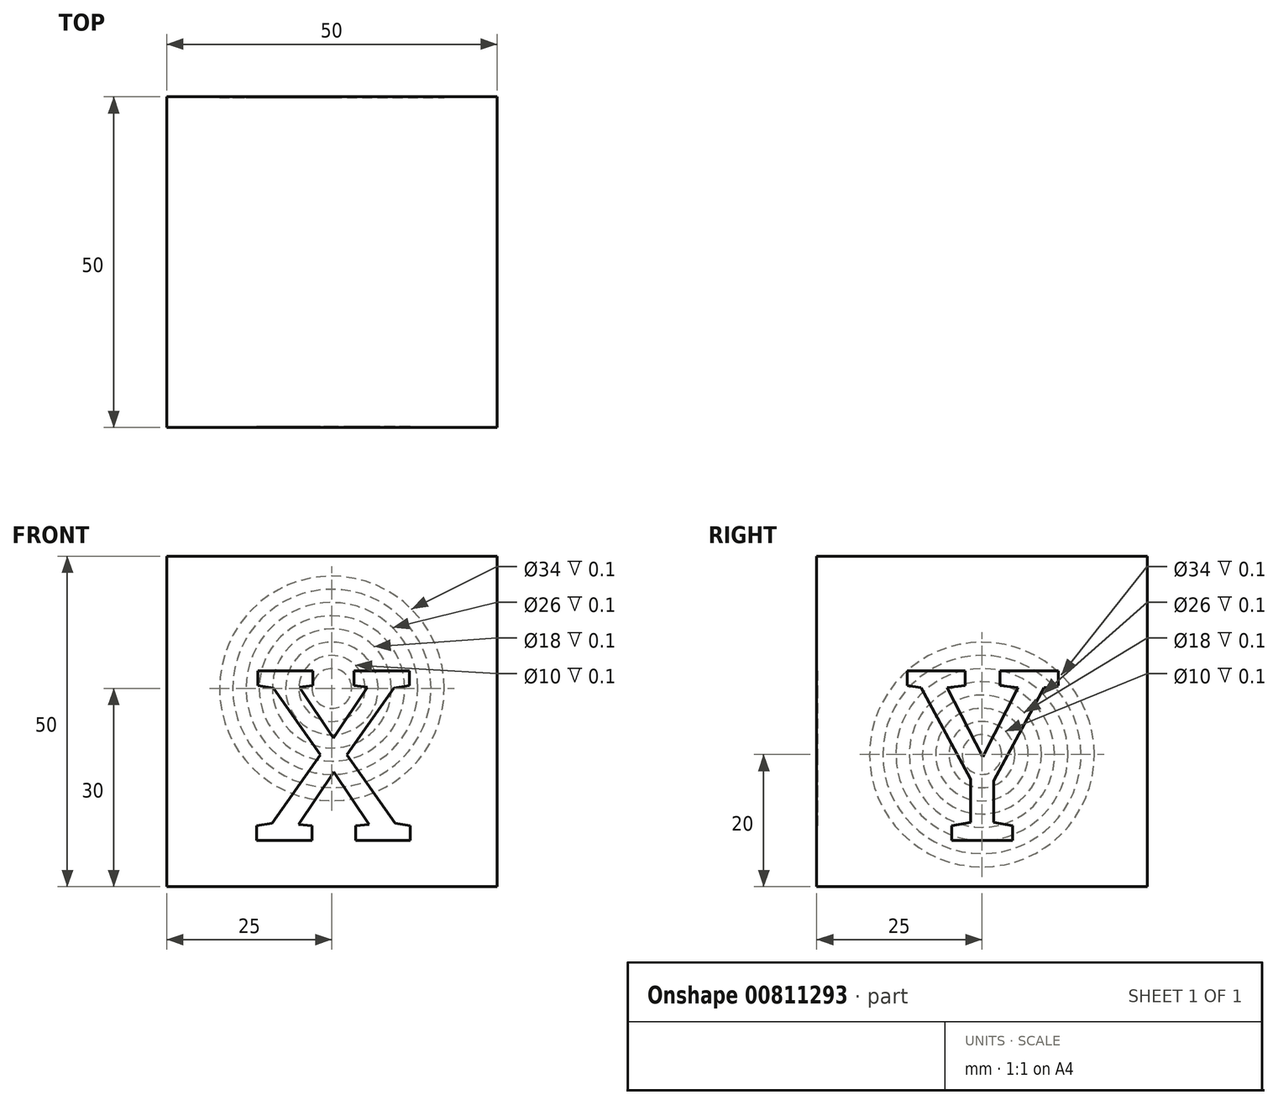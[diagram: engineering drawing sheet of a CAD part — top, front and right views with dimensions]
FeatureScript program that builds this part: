
annotation { "Feature Type Name" : "Feature", "Feature Type Description" : "" }
export const myFeature = defineFeature(function(context is Context, id is Id, definition is map)
    precondition{}
    {
        {
            var Q0;
            Q0=qCreatedBy(makeId("Top.planeOp"),FACE);
            var sketch = newSketch(context, id + "F0", { "sketchPlane" : qUnion([Q0])});
            skLineSegment(sketch, "E0.bottom", {"start": v(-25, 25) * mm, "end": v(25, 25) * mm});
            skLineSegment(sketch, "E0.top", {"start": v(-25, -25) * mm, "end": v(25, -25) * mm});
            skLineSegment(sketch, "E0.left", {"start": v(-25, 25) * mm, "end": v(-25, -25) * mm});
            skLineSegment(sketch, "E0.right", {"start": v(25, 25) * mm, "end": v(25, -25) * mm});
            skPoint(sketch, "E0.middle", {"position": v(0, 0) * mm});
            skSolve(sketch);
        }
        {
            var Q0;
            Q0 = qSketchRegion(id + "F0", true);
            extrude(context, id + "F1", {"entities" : qUnion([Q0]), "depth" : 50 * mm, "offsetDistance" : 25 * mm});
        }
        {
            var Q0;
            Q0=makeQuery(id+"F1.opExtrude","SWEPT_FACE",FACE,{"disambiguationData":[OSD([sQuery(id+"F0.wireOp",EDGE,"E0.top")])]});
            var sketch = newSketch(context, id + "F2", { "sketchPlane" : qUnion([Q0])});
            skText(sketch, "E1", { "text": "X", "fontName": "RobotoSlab-Regular.ttf"});
            skLineSegment(sketch, "E2", {"start": v(0, 50) * mm, "end": v(0, 43) * mm});
            skLineSegment(sketch, "E3", {"start": v(0, 0) * mm, "end": v(0, 7) * mm, "construction": true});
            const initialGuessF2  = {"E1": [-0.01212, 0.007, 1, 0, 0.026]};
            skSetInitialGuess(sketch, initialGuessF2);
            skSolve(sketch);
        }
        {
            var Q0;
            Q0=makeQuery(id+"F2.imprint","IMPRINT",FACE,{"disambiguationData":[TD([[makeQuery(id+"F2.imprint","IMPRINT",EDGE,{"derivedFrom":sQuery(id+"F2.wireOp",EDGE,"E1.sketch_text.stroke-0")}),-1.0]])]});
            extrude(context, id + "F3", {"entities" : qUnion([Q0]), "operationType" : NewBodyOperationType.REMOVE, "oppositeDirection" : true, "depth" : 0.1 * mm, "offsetDistance" : 25 * mm});
        }
        {
            var Q0;
            Q0=makeQuery(id+"F1.opExtrude","SWEPT_FACE",FACE,{"disambiguationData":[OSD([sQuery(id+"F0.wireOp",EDGE,"E0.bottom")])]});
            var sketch = newSketch(context, id + "F4", { "sketchPlane" : qUnion([Q0])});
            skCircle(sketch, "E4", {"center": v(0, 30) * mm, "radius": 9 * mm});
            skCircle(sketch, "E5", {"center": v(0, 30) * mm, "radius": 7 * mm});
            skCircle(sketch, "E6", {"center": v(0, 30) * mm, "radius": 3 * mm});
            skCircle(sketch, "E7", {"center": v(0, 30) * mm, "radius": 5 * mm});
            skCircle(sketch, "E8", {"center": v(0, 30) * mm, "radius": 13 * mm});
            skCircle(sketch, "E9", {"center": v(0, 30) * mm, "radius": 11 * mm});
            skCircle(sketch, "E10", {"center": v(0, 30) * mm, "radius": 17 * mm});
            skCircle(sketch, "E11", {"center": v(0, 30) * mm, "radius": 15 * mm});
            skSolve(sketch);
        }
        {
            var Q0;
            Q0=makeQuery(id+"F4.imprint","IMPRINT",FACE,{"disambiguationData":[TD([[makeQuery(id+"F4.imprint","IMPRINT",EDGE,{"derivedFrom":sQuery(id+"F4.wireOp",EDGE,"E6")}),-1.0]])]});
            var Q1;
            Q1=makeQuery(id+"F4.imprint","IMPRINT",FACE,{"disambiguationData":[TD([[makeQuery(id+"F4.imprint","IMPRINT",EDGE,{"derivedFrom":sQuery(id+"F4.wireOp",EDGE,"E4")}),1.0]])]});
            var Q2;
            Q2=makeQuery(id+"F4.imprint","IMPRINT",FACE,{"disambiguationData":[TD([[makeQuery(id+"F4.imprint","IMPRINT",EDGE,{"derivedFrom":sQuery(id+"F4.wireOp",EDGE,"E8")}),1.0]])]});
            var Q3;
            Q3=makeQuery(id+"F4.imprint","IMPRINT",FACE,{"disambiguationData":[TD([[makeQuery(id+"F4.imprint","IMPRINT",EDGE,{"derivedFrom":sQuery(id+"F4.wireOp",EDGE,"E10")}),1.0]])]});
            extrude(context, id + "F5", {"entities" : qUnion([Q0, Q1, Q2, Q3]), "operationType" : NewBodyOperationType.REMOVE, "oppositeDirection" : true, "depth" : 0.1 * mm, "offsetDistance" : 25 * mm});
        }
        {
            var Q0;
            Q0=makeQuery(id+"F1.opExtrude","SWEPT_FACE",FACE,{"disambiguationData":[OSD([sQuery(id+"F0.wireOp",EDGE,"E0.right")])]});
            var sketch = newSketch(context, id + "F6", { "sketchPlane" : qUnion([Q0])});
            skText(sketch, "E12", { "text": "Y", "fontName": "RobotoSlab-Regular.ttf"});
            const initialGuessF6  = {"E12": [-0.0123, 0.007, 1, 0, 0.026]};
            skSetInitialGuess(sketch, initialGuessF6);
            skSolve(sketch);
        }
        {
            var Q0;
            Q0=makeQuery(id+"F6.imprint","IMPRINT",FACE,{"disambiguationData":[TD([[makeQuery(id+"F6.imprint","IMPRINT",EDGE,{"derivedFrom":sQuery(id+"F6.wireOp",EDGE,"E12.sketch_text.stroke-0")}),-1.0]])]});
            extrude(context, id + "F7", {"entities" : qUnion([Q0]), "operationType" : NewBodyOperationType.REMOVE, "oppositeDirection" : true, "depth" : 0.1 * mm, "offsetDistance" : 25 * mm});
        }
        {
            var Q0;
            Q0=makeQuery(id+"F1.opExtrude","SWEPT_FACE",FACE,{"disambiguationData":[OSD([sQuery(id+"F0.wireOp",EDGE,"E0.left")])]});
            var sketch = newSketch(context, id + "F8", { "sketchPlane" : qUnion([Q0])});
            skCircle(sketch, "E13", {"center": v(0, 20) * mm, "radius": 9 * mm});
            skCircle(sketch, "E14", {"center": v(0, 20) * mm, "radius": 7 * mm});
            skCircle(sketch, "E15", {"center": v(0, 20) * mm, "radius": 3 * mm});
            skCircle(sketch, "E16", {"center": v(0, 20) * mm, "radius": 5 * mm});
            skCircle(sketch, "E17", {"center": v(0, 20) * mm, "radius": 13 * mm});
            skCircle(sketch, "E18", {"center": v(0, 20) * mm, "radius": 11 * mm});
            skCircle(sketch, "E19", {"center": v(0, 20) * mm, "radius": 17 * mm});
            skCircle(sketch, "E20", {"center": v(0, 20) * mm, "radius": 15 * mm});
            skSolve(sketch);
        }
        {
            var Q0;
            Q0=makeQuery(id+"F8.imprint","IMPRINT",FACE,{"disambiguationData":[TD([[makeQuery(id+"F8.imprint","IMPRINT",EDGE,{"derivedFrom":sQuery(id+"F8.wireOp",EDGE,"E15")}),-1.0]])]});
            var Q1;
            Q1=makeQuery(id+"F8.imprint","IMPRINT",FACE,{"disambiguationData":[TD([[makeQuery(id+"F8.imprint","IMPRINT",EDGE,{"derivedFrom":sQuery(id+"F8.wireOp",EDGE,"E13")}),1.0]])]});
            var Q2;
            Q2=makeQuery(id+"F8.imprint","IMPRINT",FACE,{"disambiguationData":[TD([[makeQuery(id+"F8.imprint","IMPRINT",EDGE,{"derivedFrom":sQuery(id+"F8.wireOp",EDGE,"E17")}),1.0]])]});
            var Q3;
            Q3=makeQuery(id+"F8.imprint","IMPRINT",FACE,{"disambiguationData":[TD([[makeQuery(id+"F8.imprint","IMPRINT",EDGE,{"derivedFrom":sQuery(id+"F8.wireOp",EDGE,"E19")}),1.0]])]});
            extrude(context, id + "F9", {"entities" : qUnion([Q0, Q1, Q2, Q3]), "operationType" : NewBodyOperationType.REMOVE, "oppositeDirection" : true, "depth" : 0.1 * mm, "offsetDistance" : 25 * mm});
        }
    });
